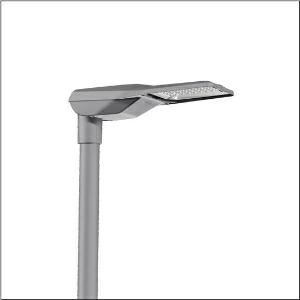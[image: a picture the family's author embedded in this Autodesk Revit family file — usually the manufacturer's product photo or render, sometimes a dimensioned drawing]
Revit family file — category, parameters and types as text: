
# Revit family: streetlight_sl_21_iq_mini___pl52_5xe2h41d08hb_c209
name_source: partatom
category: Lighting Fixtures
units: mm (PartAtom-declared; Revit-internal decimal feet)

## family parameters
Cut with Voids When Loaded = No
Host = Face
Light Source = No
Part Type = Normal
Room Calculation Point = No
Round Connector Dimension = Use Diameter
Shared = No

## types (1)
- --- (1 x LED, 9690 lm, 70.9 W, 4000K)
    Apparent Load = 71 VA
    CIE Flux Codes = 27 59 98 100 100
    Color Rendering = 70
    Color Temperature = 4000K
    Default Elevation = 1800 mm
    Description = Streetlight SL 21 iQ mini, mast luminaire, primary light control with lens, of PMMA, primary optical cover: cover, of toughened safety glass, transparent, light distribution: PL52, light emission: direct distribution, primary light characteristic: asymmetric, installation type: post-top, side-entry, LED, High Power LED, rated luminous flux: 9.690lm, luminous efficacy: 137lm/W, light colour: 740, colour temperature: 4000K, control: Auto-Match, Temp-Guard, Lumen-Switch, Night-Set, Smart-Wire, Light-Fading, Desk-Remote (wireless, voltage-free reading and setting of iQ features in the workshop via application-optimized NFC function/RFID function), optimised constant luminous flux control (CLO 2.0), presetting dimming linear, mains connection: 220..240V, AC, 50/60Hz, start of lifetime: 71W, end of service life: 75W, reduction: 31W, luminaire housing, of diecast aluminium, powder-coated, Siteco® metallic grey (DB 702S), corrosivity category C5 mid according to DIN EN ISO 12944, please order mast flange separately, inclination adjustable: 0°, 5°, 10°, 15°, sealing non-destructively replaceable, multi-level sealing system, length: 628mm, width: 235mm, height: 110mm, mast flange for spigot size: 42mm (side-entry): 5XC10008XM4, 60/48mm (side-entry/post-top): 5XC10108XM2, 76/60mm (side-entry/post-top): 5XC10108XM1, protection rating (complete): IP66, insulation class (complete): insulation class II (safety insulation), certification: CE, ENEC, ENEC+, VDE, impact resistance: IK09, permissible operating ambient temperature for outdoor applications: -40..+50°C, standard-compliant lighting for roads and squares, packaging unit: 1 piece

Light Distribution: PL52
    Height = 110 mm
    Lamp = 1 x LED
    Lamp Light Flux = 9690 lm
    Lamp Power = 70.9 W
    Lamp count = 1
    Length = 625 mm
    Luminous efficacy = 137 lm/W
    Manufacturer = Siteco
    ModVariant = No
    Model = 5XE2H41D08HB
    Number of Poles = 1
    OnlyDefault = Yes
    Power Factor = 1
    Product Name = Streetlight SL 21 iQ mini | PL52
    Product group = mast luminaire | pylon top
    ProductGroupID = 6100
    Protection Class = Protection class II
    Protection Degree = IP 66
    RLX_Detail_Level = 1
    RLX_Emergency_Light_Flux = 0 lm
    RLX_Emergency_Type = 0
    RLX_Emergency_Type_DB = No
    RlxData = <blob elided: 101921 chars, md5=3e65d323>
    Socket = socket
    Standby Power = 0 W
    System Light Flux = 9690 lm
    System Power = 71 W
    Type Comments = factory setting: luminous flux: 100 % | dim-lin: 254 | 711 mA
    Type Image = l_1003519.jpg
    URL = http://relux.com
    VarID = @adj_090723
    Voltage = 0 V
    Weight = 0.00 kg
    Width = 234 mm

## geometry (parser evidence)
native form markers: Blend x4, Sweep x10
no freeform markers — native parametric forms only
